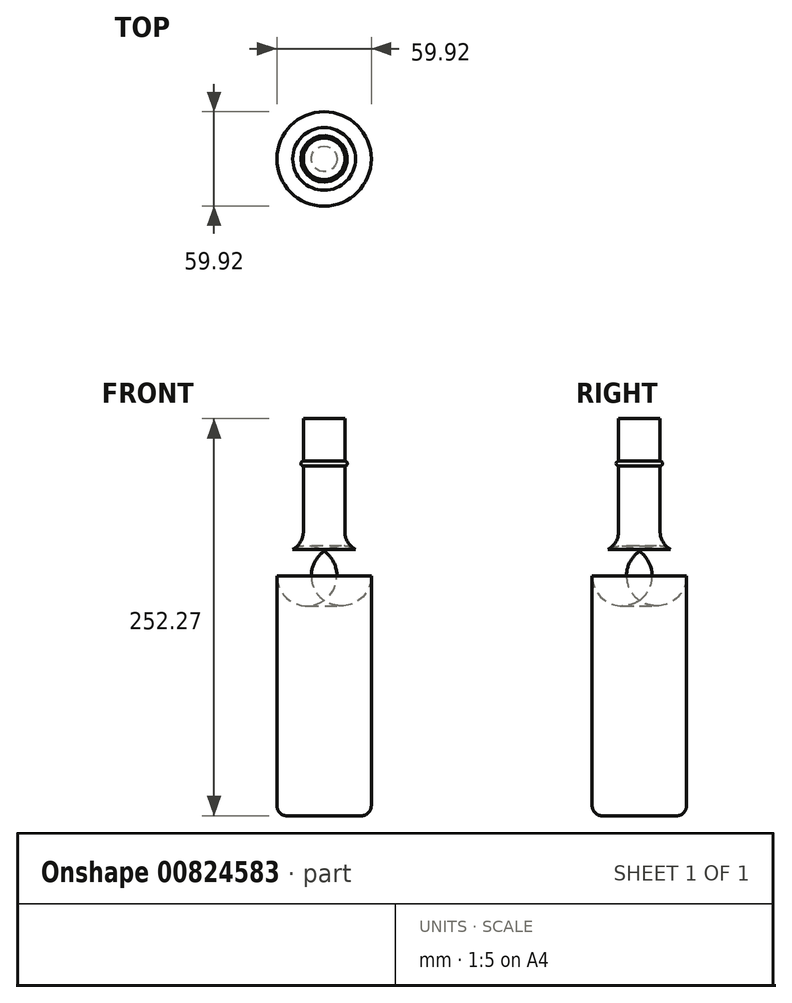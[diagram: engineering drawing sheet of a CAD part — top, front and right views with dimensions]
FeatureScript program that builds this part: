
annotation { "Feature Type Name" : "Feature", "Feature Type Description" : "" }
export const myFeature = defineFeature(function(context is Context, id is Id, definition is map)
    precondition{}
    {
        {
            var Q0;
            Q0=qCreatedBy(makeId("Front.planeOp"),FACE);
            var sketch = newSketch(context, id + "F0", { "sketchPlane" : qUnion([Q0])});
            skLineSegment(sketch, "E0", {"start": v(0, 0) * mm, "end": v(23.6, 0) * mm});
            skLineSegment(sketch, "E1", {"start": v(29.96, 6.35) * mm, "end": v(29.96, 152.4) * mm});
            skLineSegment(sketch, "E2", {"start": v(13.2, 180.38) * mm, "end": v(13.2, 222.11) * mm});
            skArc(sketch, "E3", {"start": v(13.2, 222.11) * mm, "mid": v(14.72, 223.7) * mm, "end": v(13.2, 225.28) * mm});
            skLineSegment(sketch, "E4", {"start": v(13.2, 225.28) * mm, "end": v(13.2, 252.27) * mm});
            skLineSegment(sketch, "E5", {"start": v(13.2, 252.27) * mm, "end": v(0, 252.27) * mm});
            skArc(sketch, "E6", {"start": v(19.9, 169.2) * mm, "mid": v(27.25, 162.18) * mm, "end": v(29.96, 152.4) * mm});
            skPoint(sketch, "E7.visualSharp", {"position": v(13.2, 171.31) * mm});
            skArc(sketch, "E7.filletArc", {"start": v(13.2, 180.38) * mm, "mid": v(15.01, 173.86) * mm, "end": v(19.9, 169.2) * mm});
            skPoint(sketch, "E8.visualSharp", {"position": v(29.96, 0) * mm});
            skArc(sketch, "E8.filletArc", {"start": v(23.6, 0) * mm, "mid": v(28.1, 1.86) * mm, "end": v(29.96, 6.35) * mm});
            skSolve(sketch);
        }
        {
            var Q0;
            Q0=qCreatedBy(makeId("Front.planeOp"),FACE);
            var sketch = newSketch(context, id + "F1", { "sketchPlane" : qUnion([Q0])});
            skLineSegment(sketch, "E9", {"start": v(0, 285.04) * mm, "end": v(0, -87.05) * mm, "construction": true});
            skSolve(sketch);
        }
        {
            var Q0;
            Q0 = qConstructionFilter(qBodyType(qCreatedBy(id + "F0" ,EDGE), BodyType.WIRE), ConstructionObject.NO);
            var Q1;
            Q1=sQuery(id+"F1.wireOp",EDGE,"E9");
            revolve(context, id + "F2", {"bodyType" : ToolBodyType.SURFACE, "surfaceOperationType" : NewSurfaceOperationType.NEW, "surfaceEntities" : qUnion([Q0]), "axis" : qUnion([Q1]), "revolveType" : RevolveType.FULL});
        }
    });
